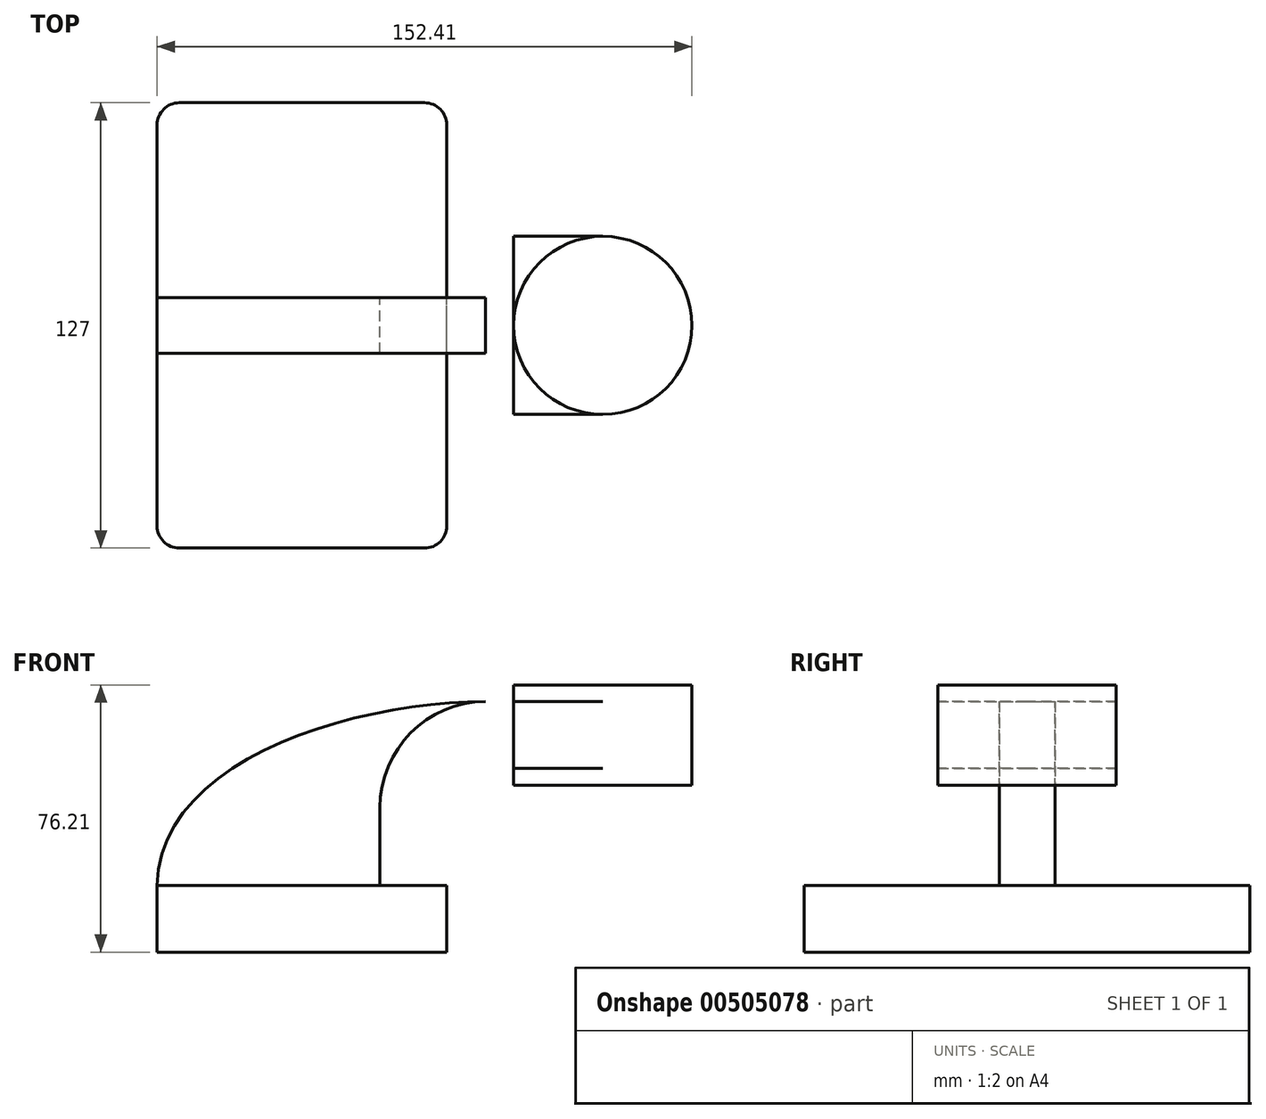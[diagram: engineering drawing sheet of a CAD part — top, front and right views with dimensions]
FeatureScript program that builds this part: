
annotation { "Feature Type Name" : "Feature", "Feature Type Description" : "" }
export const myFeature = defineFeature(function(context is Context, id is Id, definition is map)
    precondition{}
    {
        {
            var Q0;
            Q0=qCreatedBy(makeId("Front.planeOp"),FACE);
            var sketch = newSketch(context, id + "F0", { "sketchPlane" : qUnion([Q0])});
            skLineSegment(sketch, "E0.bottom", {"start": v(41.28, 9.53) * mm, "end": v(-41.28, 9.53) * mm});
            skLineSegment(sketch, "E0.top", {"start": v(41.28, -9.52) * mm, "end": v(-41.28, -9.52) * mm});
            skLineSegment(sketch, "E0.left", {"start": v(41.28, 9.53) * mm, "end": v(41.28, -9.52) * mm});
            skLineSegment(sketch, "E0.right", {"start": v(-41.28, 9.53) * mm, "end": v(-41.28, -9.52) * mm});
            skPoint(sketch, "E0.middle", {"position": v(0, 0) * mm});
            skLineSegment(sketch, "E1.bottom", {"start": v(60.33, 38.1) * mm, "end": v(111.13, 38.1) * mm});
            skLineSegment(sketch, "E1.top", {"start": v(60.33, 66.68) * mm, "end": v(111.13, 66.68) * mm});
            skLineSegment(sketch, "E1.left", {"start": v(60.33, 38.1) * mm, "end": v(60.33, 66.68) * mm});
            skLineSegment(sketch, "E1.right", {"start": v(111.13, 38.1) * mm, "end": v(111.13, 66.68) * mm});
            skPoint(sketch, "E1.middle", {"position": v(85.73, 52.39) * mm});
            skArc(sketch, "E2", {"start": v(41.28, 31.65) * mm, "mid": v(44.56, 39.59) * mm, "end": v(52.5, 42.88) * mm});
            skLineSegment(sketch, "E3", {"start": v(52.5, 42.88) * mm, "end": v(85.72, 42.88) * mm});
            skLineSegment(sketch, "E4", {"start": v(41.28, 31.65) * mm, "end": v(41.28, 9.53) * mm});
            skLineSegment(sketch, "E5.0", {"start": v(22.22, 31.65) * mm, "end": v(22.22, 9.53) * mm});
            skArc(sketch, "E5.1", {"start": v(22.23, 31.65) * mm, "mid": v(31.1, 53.06) * mm, "end": v(52.5, 61.93) * mm});
            skLineSegment(sketch, "E5.2", {"start": v(52.5, 61.93) * mm, "end": v(85.72, 61.93) * mm});
            skLineSegment(sketch, "E6", {"start": v(85.73, 66.68) * mm, "end": v(85.73, 38.1) * mm});
            skFitSpline(sketch, "E7", {"points": [v(-41.28, 9.52) * mm, v(52.5, 61.93) * mm], "startDerivative": vector(1.98, 107.69) * mm, "endDerivative": vector(114.05, 0.33) * mm});
            skSolve(sketch);
        }
        {
            var Q0;
            Q0=makeQuery(id+"F0.imprint","IMPRINT",FACE,{"disambiguationData":[TD([[makeQuery(id+"F0.imprint","IMPRINT",EDGE,{"derivedFrom":sQuery(id+"F0.wireOp",EDGE,"E0.top")}),-1.0]])]});
            extrude(context, id + "F1", {"entities" : qUnion([Q0]), "endBound" : BoundingType.SYMMETRIC, "depth" : 127 * mm});
        }
        {
            var Q0;
            {var subQ0=sQuery(id+"F0.wireOp",EDGE,"E3");var subQ1=sQuery(id+"F0.wireOp",EDGE,"E1.left");var subQ2=makeQuery(id+"F0.imprint","INTERSECT",VERTEX,{"derivedFrom":[subQ1,subQ0]});Q0=makeQuery(id+"F0.imprint","IMPRINT",FACE,{"disambiguationData":[TD([[makeQuery(id+"F0.imprint","IMPRINT",EDGE,{"disambiguationData":[TD([[subQ2,-1.0]])],"derivedFrom":subQ1}),-1.0]])]});}
            var Q1;
            {var subQ1=sQuery(id+"F0.wireOp",EDGE,"E2");Q1=makeQuery(id+"F0.imprint","IMPRINT",FACE,{"disambiguationData":[TD([[makeQuery(id+"F0.imprint","IMPRINT",EDGE,{"derivedFrom":subQ1}),1.0]])]});}
            extrude(context, id + "F2", {"entities" : qUnion([Q0, Q1]), "operationType" : NewBodyOperationType.ADD, "endBound" : BoundingType.SYMMETRIC, "depth" : 50.8 * mm});
        }
        {
            var Q0;
            {var subQ3=sQuery(id+"F0.wireOp",EDGE,"E5.0");Q0=makeQuery(id+"F0.imprint","IMPRINT",FACE,{"disambiguationData":[TD([[makeQuery(id+"F0.imprint","IMPRINT",EDGE,{"derivedFrom":subQ3}),-1.0]])]});}
            extrude(context, id + "F3", {"entities" : qUnion([Q0]), "operationType" : NewBodyOperationType.ADD, "endBound" : BoundingType.SYMMETRIC, "depth" : 15.88 * mm});
        }
        {
            var Q0;
            {var subQ0=sQuery(id+"F0.wireOp",EDGE,"E1.right");Q0=makeQuery(id+"F0.imprint","IMPRINT",FACE,{"disambiguationData":[TD([[makeQuery(id+"F0.imprint","IMPRINT",EDGE,{"derivedFrom":subQ0}),1.0]])]});}
            var Q1;
            Q1=sQuery(id+"F0.wireOp",EDGE,"E6");
            revolve(context, id + "F4", {"operationType" : NewBodyOperationType.ADD, "entities" : qUnion([Q0]), "axis" : qUnion([Q1]), "revolveType" : RevolveType.FULL});
        }
        {
            var Q0;
            Q0=makeQuery(id+"F1.opExtrude","CAP_EDGE",EDGE,{"disambiguationData":[OSD([sQuery(id+"F0.wireOp",EDGE,"E0.left")])],"isStart":false});
            var Q1;
            Q1=makeQuery(id+"F1.opExtrude","CAP_EDGE",EDGE,{"disambiguationData":[OSD([sQuery(id+"F0.wireOp",EDGE,"E0.right")])],"isStart":false});
            var Q2;
            Q2=makeQuery(id+"F1.opExtrude","CAP_EDGE",EDGE,{"disambiguationData":[OSD([sQuery(id+"F0.wireOp",EDGE,"E0.left")])],"isStart":true});
            var Q3;
            Q3=makeQuery(id+"F1.opExtrude","CAP_EDGE",EDGE,{"disambiguationData":[OSD([sQuery(id+"F0.wireOp",EDGE,"E0.right")])],"isStart":true});
            fillet(context, id + "F5", {"entities" : qUnion([Q0, Q1, Q2, Q3]), "radius" : 6.35 * mm, "tangentPropagation" : true, "allowEdgeOverflow" : false});
        }
    });
